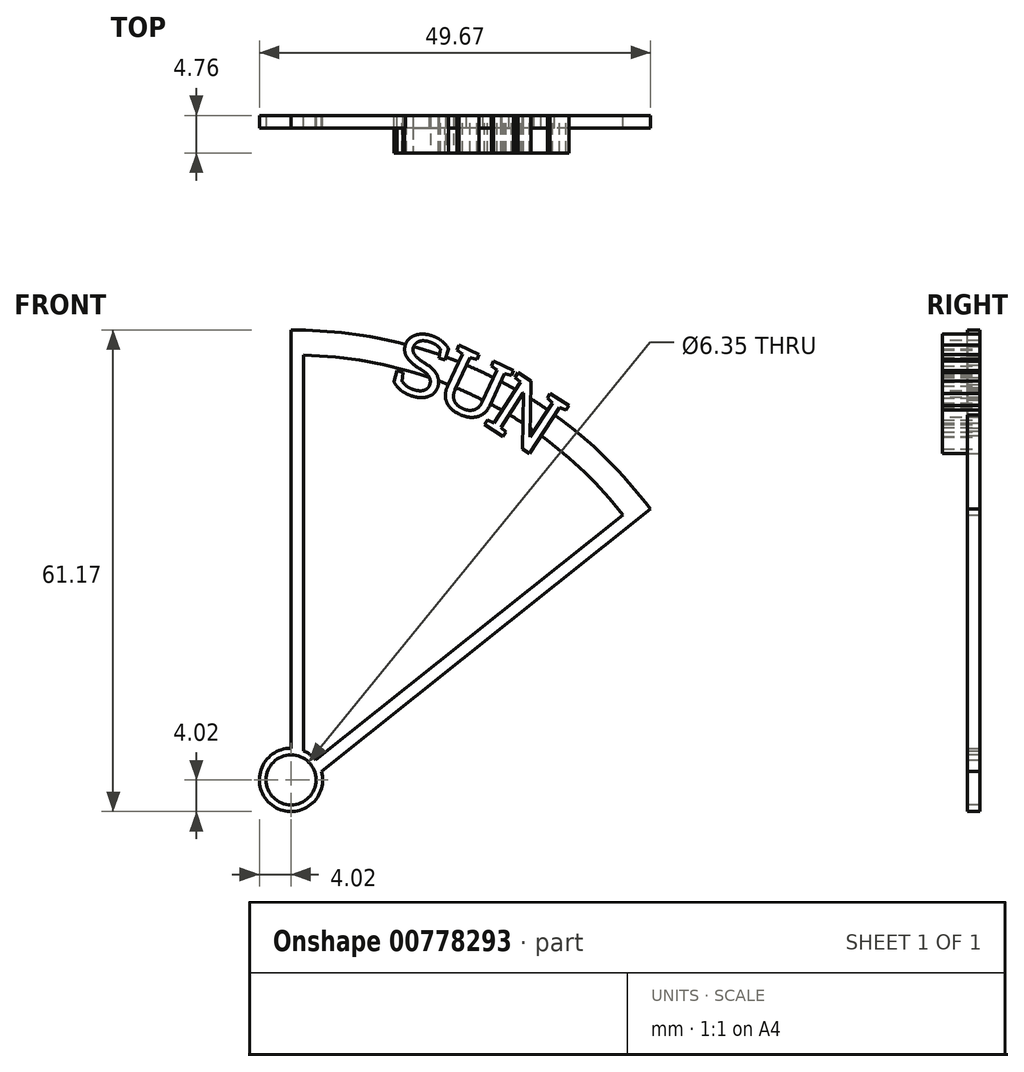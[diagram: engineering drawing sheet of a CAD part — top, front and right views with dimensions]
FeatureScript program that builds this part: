
annotation { "Feature Type Name" : "Feature", "Feature Type Description" : "" }
export const myFeature = defineFeature(function(context is Context, id is Id, definition is map)
    precondition{}
    {
        {
            var Q0;
            Q0=qCreatedBy(makeId("Front.planeOp"),FACE);
            var sketch = newSketch(context, id + "F0", { "sketchPlane" : qUnion([Q0])});
            skCircle(sketch, "E0", {"center": v(0, 0) * mm, "radius": 59.18 * mm, "construction": true});
            skCircle(sketch, "E1", {"center": v(0, 0) * mm, "radius": 50.8 * mm, "construction": true});
            skLineSegment(sketch, "E2", {"start": v(0, 0) * mm, "end": v(0, 59.18) * mm, "construction": true});
            skLineSegment(sketch, "E3", {"start": v(0, 0) * mm, "end": v(46.26, 36.9) * mm, "construction": true});
            skLineSegment(sketch, "E4", {"start": v(0, 0) * mm, "end": v(17.8, 56.44) * mm, "construction": true});
            skLineSegment(sketch, "E5", {"start": v(0, 0) * mm, "end": v(25.02, 53.63) * mm, "construction": true});
            skLineSegment(sketch, "E6", {"start": v(0, 0) * mm, "end": v(32.24, 49.63) * mm, "construction": true});
            skText(sketch, "E7", { "text": "S", "fontName": "RobotoSlab-Regular.ttf"});
            skText(sketch, "E8", { "text": "U", "fontName": "RobotoSlab-Regular.ttf"});
            skText(sketch, "E9", { "text": "N", "fontName": "RobotoSlab-Regular.ttf"});
            skLineSegment(sketch, "E10", {"start": v(0, 0) * mm, "end": v(14.53, 57.47) * mm, "construction": true});
            skLineSegment(sketch, "E11", {"start": v(0, 0) * mm, "end": v(35.9, 47.25) * mm, "construction": true});
            const initialGuessF0  = {"E7": [0.01214, 0.0499, 0.95366, -0.30089, 0.00794], "E8": [0.01774, 0.04827, 0.90623, -0.4228, 0.00794], "E9": [0.02425, 0.04535, 0.83857, -0.5448, 0.00794]};
            skSetInitialGuess(sketch, initialGuessF0);
            skSolve(sketch);
        }
        {
            var Q0;
            Q0 = qSketchRegion(id + "F0", true);
            extrude(context, id + "F1", {"entities" : qUnion([Q0]), "depth" : 4.76 * mm, "offsetDistance" : 25.4 * mm});
        }
        {
            var Q0;
            Q0=qCreatedBy(makeId("Front.planeOp"),FACE);
            var sketch = newSketch(context, id + "F2", { "sketchPlane" : qUnion([Q0])});
            skCircle(sketch, "E12", {"center": v(0, 0) * mm, "radius": 4.13 * mm, "construction": true});
            skCircle(sketch, "E13", {"center": v(0, 0) * mm, "radius": 4.02 * mm});
            skCircle(sketch, "E14", {"center": v(0, 0) * mm, "radius": 57.15 * mm, "construction": true});
            skCircle(sketch, "E15", {"center": v(0, 0) * mm, "radius": 53.98 * mm, "construction": true});
            skLineSegment(sketch, "E16", {"start": v(0, 0) * mm, "end": v(0, 57.15) * mm, "construction": true});
            skLineSegment(sketch, "E17", {"start": v(0, 0) * mm, "end": v(42.2, 33.66) * mm, "construction": true});
            skLineSegment(sketch, "E18", {"start": v(1.59, 53.95) * mm, "end": v(1.59, 3.7) * mm, "construction": true});
            skLineSegment(sketch, "E19", {"start": v(45.65, 34.38) * mm, "end": v(3.88, 1.06) * mm, "construction": true});
            skLineSegment(sketch, "E20", {"start": v(0, 57.15) * mm, "end": v(0, 0) * mm});
            skLineSegment(sketch, "E21", {"start": v(42.2, 33.66) * mm, "end": v(0, 0) * mm});
            skLineSegment(sketch, "E22", {"start": v(45.65, 34.38) * mm, "end": v(3.88, 1.06) * mm});
            skLineSegment(sketch, "E23", {"start": v(1.59, 53.95) * mm, "end": v(1.59, 3.7) * mm});
            skArc(sketch, "E24", {"start": v(42.2, 33.66) * mm, "mid": v(24.16, 48.35) * mm, "end": v(1.59, 53.95) * mm});
            skArc(sketch, "E25", {"start": v(45.65, 34.38) * mm, "mid": v(25.53, 51.2) * mm, "end": v(0, 57.15) * mm});
            skSolve(sketch);
        }
        {
            var Q0;
            {var subQ0=sQuery(id+"F2.wireOp",EDGE,"E22");Q0=makeQuery(id+"F2.imprint","IMPRINT",FACE,{"disambiguationData":[TD([[makeQuery(id+"F2.imprint","IMPRINT",EDGE,{"derivedFrom":subQ0}),-1.0]])]});}
            var Q1;
            {var subQ0=sQuery(id+"F2.wireOp",EDGE,"E21");var subQ1=sQuery(id+"F2.wireOp",EDGE,"E20");var subQ2=makeQuery(id+"F2.imprint","INTERSECT",VERTEX,{"derivedFrom":[subQ1,subQ0]});Q1=makeQuery(id+"F2.imprint","IMPRINT",FACE,{"disambiguationData":[TD([[makeQuery(id+"F2.imprint","IMPRINT",EDGE,{"disambiguationData":[TD([[subQ2,1.0]])],"derivedFrom":subQ1}),-1.0]])]});}
            var Q2;
            {var subQ0=sQuery(id+"F2.wireOp",EDGE,"E21");var subQ1=sQuery(id+"F2.wireOp",EDGE,"E20");var subQ2=makeQuery(id+"F2.imprint","INTERSECT",VERTEX,{"derivedFrom":[subQ1,subQ0]});Q2=makeQuery(id+"F2.imprint","IMPRINT",FACE,{"disambiguationData":[TD([[makeQuery(id+"F2.imprint","IMPRINT",EDGE,{"disambiguationData":[TD([[subQ2,1.0]])],"derivedFrom":subQ1}),1.0]])]});}
            extrude(context, id + "F3", {"entities" : qUnion([Q0, Q1, Q2]), "operationType" : NewBodyOperationType.ADD, "depth" : 1.59 * mm, "offsetDistance" : 25.4 * mm});
        }
        {
            var Q0;
            {var subQ0=sQuery(id+"F2.wireOp",EDGE,"E23");var subQ1=sQuery(id+"F2.wireOp",EDGE,"E22");var subQ2=sQuery(id+"F2.wireOp",EDGE,"E20");var subQ3=sQuery(id+"F2.wireOp",EDGE,"E21");var subQ4=sQuery(id+"F2.wireOp",EDGE,"E13");var subQ5=sQuery(id+"F2.wireOp",EDGE,"E24");var subQ6=sQuery(id+"F2.wireOp",EDGE,"E25");Q0=makeQuery(id+"F3.boolean.opBoolean","SPLIT",FACE,{"disambiguationData":[TD([makeQuery(id+"F1.opExtrude","SWEPT_FACE",FACE,{"disambiguationData":[OSD([sQuery(id+"F0.wireOp",EDGE,"E7.sketch_text.stroke-21")])]})])],"derivedFrom":makeQuery(id+"F3.opExtrude","CAP_FACE",FACE,{"disambiguationData":[OSD([subQ2,subQ3,subQ1,subQ0,subQ4,subQ5,subQ6])],"isStart":false})});}
            var sketch = newSketch(context, id + "F4", { "sketchPlane" : qUnion([Q0])});
            skPoint(sketch, "E26", {"position": v(0, 0) * mm});
            skSolve(sketch);
        }
        {
            var Q0;
            Q0=sQuery(id+"F4.wireOp",VERTEX,"E26");
            var Q1;
            Q1=makeQuery(id+"F1.opExtrude","SWEPT_BODY",BODY,{"disambiguationData":[OSD([sQuery(id+"F0.wireOp",EDGE,"E7.sketch_text.stroke-0"),sQuery(id+"F0.wireOp",EDGE,"E7.sketch_text.stroke-1"),sQuery(id+"F0.wireOp",EDGE,"E7.sketch_text.stroke-2"),sQuery(id+"F0.wireOp",EDGE,"E7.sketch_text.stroke-3"),sQuery(id+"F0.wireOp",EDGE,"E7.sketch_text.stroke-4"),sQuery(id+"F0.wireOp",EDGE,"E7.sketch_text.stroke-5"),sQuery(id+"F0.wireOp",EDGE,"E7.sketch_text.stroke-6"),sQuery(id+"F0.wireOp",EDGE,"E7.sketch_text.stroke-7"),sQuery(id+"F0.wireOp",EDGE,"E7.sketch_text.stroke-8"),sQuery(id+"F0.wireOp",EDGE,"E7.sketch_text.stroke-9"),sQuery(id+"F0.wireOp",EDGE,"E7.sketch_text.stroke-10"),sQuery(id+"F0.wireOp",EDGE,"E7.sketch_text.stroke-11"),sQuery(id+"F0.wireOp",EDGE,"E7.sketch_text.stroke-12"),sQuery(id+"F0.wireOp",EDGE,"E7.sketch_text.stroke-13"),sQuery(id+"F0.wireOp",EDGE,"E7.sketch_text.stroke-14"),sQuery(id+"F0.wireOp",EDGE,"E7.sketch_text.stroke-15"),sQuery(id+"F0.wireOp",EDGE,"E7.sketch_text.stroke-16"),sQuery(id+"F0.wireOp",EDGE,"E7.sketch_text.stroke-17"),sQuery(id+"F0.wireOp",EDGE,"E7.sketch_text.stroke-18"),sQuery(id+"F0.wireOp",EDGE,"E7.sketch_text.stroke-19"),sQuery(id+"F0.wireOp",EDGE,"E7.sketch_text.stroke-20"),sQuery(id+"F0.wireOp",EDGE,"E7.sketch_text.stroke-21"),sQuery(id+"F0.wireOp",EDGE,"E7.sketch_text.stroke-22"),sQuery(id+"F0.wireOp",EDGE,"E7.sketch_text.stroke-23"),sQuery(id+"F0.wireOp",EDGE,"E7.sketch_text.stroke-24"),sQuery(id+"F0.wireOp",EDGE,"E7.sketch_text.stroke-25"),sQuery(id+"F0.wireOp",EDGE,"E7.sketch_text.stroke-26"),sQuery(id+"F0.wireOp",EDGE,"E7.sketch_text.stroke-27"),sQuery(id+"F0.wireOp",EDGE,"E7.sketch_text.stroke-28"),sQuery(id+"F0.wireOp",EDGE,"E7.sketch_text.stroke-29")])]});
            hole(context, id + "F5", {"style" : HoleStyle.SIMPLE, "endStyle" : HoleEndStyle.THROUGH, "holeDiameter" : 6.35 * mm, "majorDiameter" : 6.35 * mm, "isTappedThrough" : true, "tappedDepth" : 12.7 * mm, "tapClearance" : 3, "locations" : qUnion([Q0]), "scope" : qUnion([Q1])});
        }
    });
